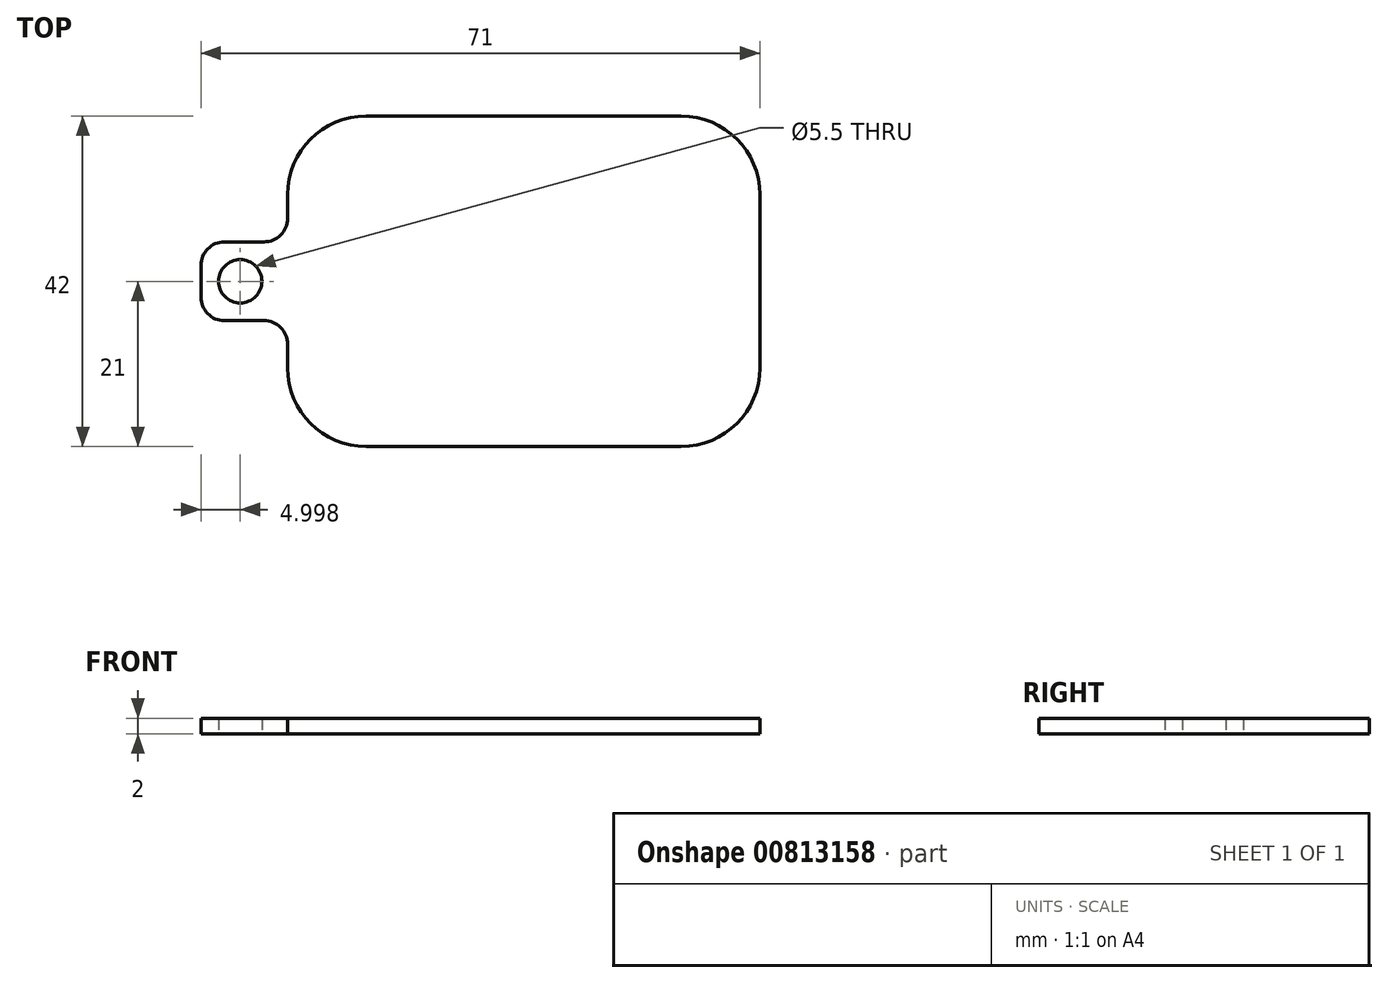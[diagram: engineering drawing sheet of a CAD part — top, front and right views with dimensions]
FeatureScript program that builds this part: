
annotation { "Feature Type Name" : "Feature", "Feature Type Description" : "" }
export const myFeature = defineFeature(function(context is Context, id is Id, definition is map)
    precondition{}
    {
        {
            var Q0;
            Q0=qCreatedBy(makeId("Top.planeOp"),FACE);
            var sketch = newSketch(context, id + "F0", { "sketchPlane" : qUnion([Q0])});
            skLineSegment(sketch, "E0.bottom", {"start": v(37.04, 21) * mm, "end": v(-2.96, 21) * mm});
            skLineSegment(sketch, "E0.top", {"start": v(37.04, -21) * mm, "end": v(-2.96, -21) * mm});
            skLineSegment(sketch, "E0.left", {"start": v(47.04, 11) * mm, "end": v(47.04, -11) * mm});
            skLineSegment(sketch, "E0.right", {"start": v(-12.96, 11) * mm, "end": v(-12.96, 8) * mm});
            skLineSegment(sketch, "E1.bottom", {"start": v(-20.96, 5) * mm, "end": v(-15.96, 5) * mm});
            skLineSegment(sketch, "E1.top", {"start": v(-20.96, -5) * mm, "end": v(-15.96, -5) * mm});
            skLineSegment(sketch, "E1.left", {"start": v(-23.96, 2) * mm, "end": v(-23.96, -2) * mm});
            skLineSegment(sketch, "E2.trimOffspring", {"start": v(-12.96, -8) * mm, "end": v(-12.96, -11) * mm});
            skPoint(sketch, "E3.visualSharp", {"position": v(-12.96, 5) * mm});
            skArc(sketch, "E3.filletArc", {"start": v(-15.96, 5) * mm, "mid": v(-13.84, 5.88) * mm, "end": v(-12.96, 8) * mm});
            skPoint(sketch, "E4.visualSharp", {"position": v(-23.96, 5) * mm});
            skArc(sketch, "E4.filletArc", {"start": v(-20.96, 5) * mm, "mid": v(-23.08, 4.12) * mm, "end": v(-23.96, 2) * mm});
            skPoint(sketch, "E5.visualSharp", {"position": v(-23.96, -5) * mm});
            skArc(sketch, "E5.filletArc", {"start": v(-23.96, -2) * mm, "mid": v(-23.08, -4.12) * mm, "end": v(-20.96, -5) * mm});
            skPoint(sketch, "E6.visualSharp", {"position": v(-12.96, -5) * mm});
            skArc(sketch, "E6.filletArc", {"start": v(-12.96, -8) * mm, "mid": v(-13.84, -5.88) * mm, "end": v(-15.96, -5) * mm});
            skPoint(sketch, "E7.visualSharp", {"position": v(-12.96, 21) * mm});
            skArc(sketch, "E7.filletArc", {"start": v(-2.96, 21) * mm, "mid": v(-10.03, 18.07) * mm, "end": v(-12.96, 11) * mm});
            skPoint(sketch, "E8.visualSharp", {"position": v(-12.96, -21) * mm});
            skArc(sketch, "E8.filletArc", {"start": v(-12.96, -11) * mm, "mid": v(-10.03, -18.07) * mm, "end": v(-2.96, -21) * mm});
            skPoint(sketch, "E9.visualSharp", {"position": v(47.04, 21) * mm});
            skArc(sketch, "E9.filletArc", {"start": v(47.04, 11) * mm, "mid": v(44.1, 18.07) * mm, "end": v(37.04, 21) * mm});
            skPoint(sketch, "E10.visualSharp", {"position": v(47.04, -21) * mm});
            skArc(sketch, "E10.filletArc", {"start": v(37.04, -21) * mm, "mid": v(44.1, -18.07) * mm, "end": v(47.04, -11) * mm});
            skCircle(sketch, "E11", {"center": v(-18.96, 0) * mm, "radius": 2.75 * mm});
            skPoint(sketch, "E11.centerSnap0", {"position": v(-23.96, 0) * mm});
            skSolve(sketch);
        }
        {
            var Q0;
            Q0=makeQuery(id+"F0.imprint","IMPRINT",FACE,{"disambiguationData":[TD([[makeQuery(id+"F0.imprint","IMPRINT",EDGE,{"derivedFrom":sQuery(id+"F0.wireOp",EDGE,"E0.bottom")}),1.0]])]});
            extrude(context, id + "F1", {"entities" : qUnion([Q0]), "depth" : 2 * mm, "offsetDistance" : 25 * mm});
        }
    });
